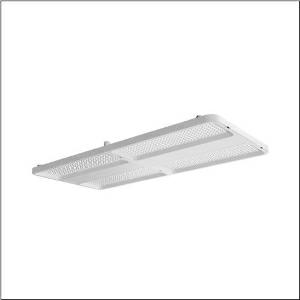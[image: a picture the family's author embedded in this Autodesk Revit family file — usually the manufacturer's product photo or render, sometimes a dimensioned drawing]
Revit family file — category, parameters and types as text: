
# Revit family: highbay_11_maxi_51hn12db4hda
name_source: partatom
category: Lighting Fixtures
units: mm (PartAtom-declared; Revit-internal decimal feet)

## family parameters
Cut with Voids When Loaded = No
Host = Face
Light Source = No
Part Type = Normal
Room Calculation Point = No
Round Connector Dimension = Use Diameter
Shared = No

## types (1)
- --- (1 x LED, 2990 lm, 15.1 W, 4000K)
    Apparent Load = 15 VA
    CIE Flux Codes = 87 98 100 100 100
    Color Rendering = 80
    Color Temperature = 4000K
    Default Elevation = 1800 mm
    Description = high bay luminaire Highbay 11 maxi; direct symmetric wide distribution, light control with lens of PMMA; UGR ≤ 19 (X = 4H | Y = 8H | S = 0.25H | reflection values 70/50/20); luminous flux: 20.000lm; light colour: 840, colour temperature: 4000K, MacAdam ≤ 2 SDCM (initial), colour rendering: CRI > 80; luminous efficacy: 210,7lm/W; rated service life: 100.000h (L95) at AT= 25°C; control: DALI 2; luminaire connection: terminal, 5-pole, max. 2.5mm² (cable entry for one cable, Ø 8.5..16mm); mains connection: 230..240V, AC/DC 0/50..60Hz; connected load: 94,9W; protection rating (complete): IP66; insulation class (complete): insulation class I (protective earthing); protection symbol: D; impact resistance: IK08; certification: CE, ENEC, VDE, UKCA; luminaire for central battery installations according to EN 60598-2-22, internal wiring halogen-free; luminaire Suitable for use in the food industry according to the specifications of IFS-Food, HACCP and/or BRC; LABS conformity tested according to VDMA 24364:2018-05; housing frame of high-performance plastic PA6, matt traffic white (RAL 9016); cover of PMMA; dimension (LxWxH): 946 x 442 x 72mm; permissible operating ambient temperature: -40..+65°C (reducing of maximum allowable ambient temperature of 5°C with ceiling mounting); packaging unit: 1 piece; (delivery without accessories; please order mounting accessories separately)
    Height = 72 mm  [stored 0.23622 ft]
    Lamp = 1 x LED
    Lamp Light Flux = 2990 lm
    Lamp Power = 15.1 W
    Lamp count = 1
    Length = 946 mm
    Luminous efficacy = 198 lm/W
    Manufacturer = Siteco
    ModVariant = No
    Model = 51HN12DB4HDA
    Mounting Place = Ceiling
    Mounting Type = Pendant
    Number of Poles = 1
    OnlyDefault = Yes
    Power Factor = 1
    Product Name = Highbay 11 maxi
    Product group = high bay luminaire
    ProductGroupID = 902
    Protection Class = Protection class I
    Protection Degree = IP 66
    RLX_Detail_Level = 1
    RLX_Emergency_Light_Flux = 0 lm
    RLX_Emergency_Type = 0
    RLX_Emergency_Type_DB = No
    RlxData = <blob elided: 127717 chars, md5=46bffeee>
    Socket = socket
    Standby Power = 0 W
    System Light Flux = 2990 lm
    System Power = 15 W
    Type Comments = : DC mode (central or group accumulator) initial emergency light level
    Type Image = l_1363244.jpg
    URL = http://relux.com
    VarID = @adj_024897
    Voltage = 0 V
    Weight = 0.00 kg
    Width = 442 mm

note: [stored X ft] marks values corroborated as IEEE doubles in the binary element streams (Revit-internal decimal feet)

## geometry (parser evidence)
native form markers: Blend x4, Sweep x9
no freeform markers — native parametric forms only
